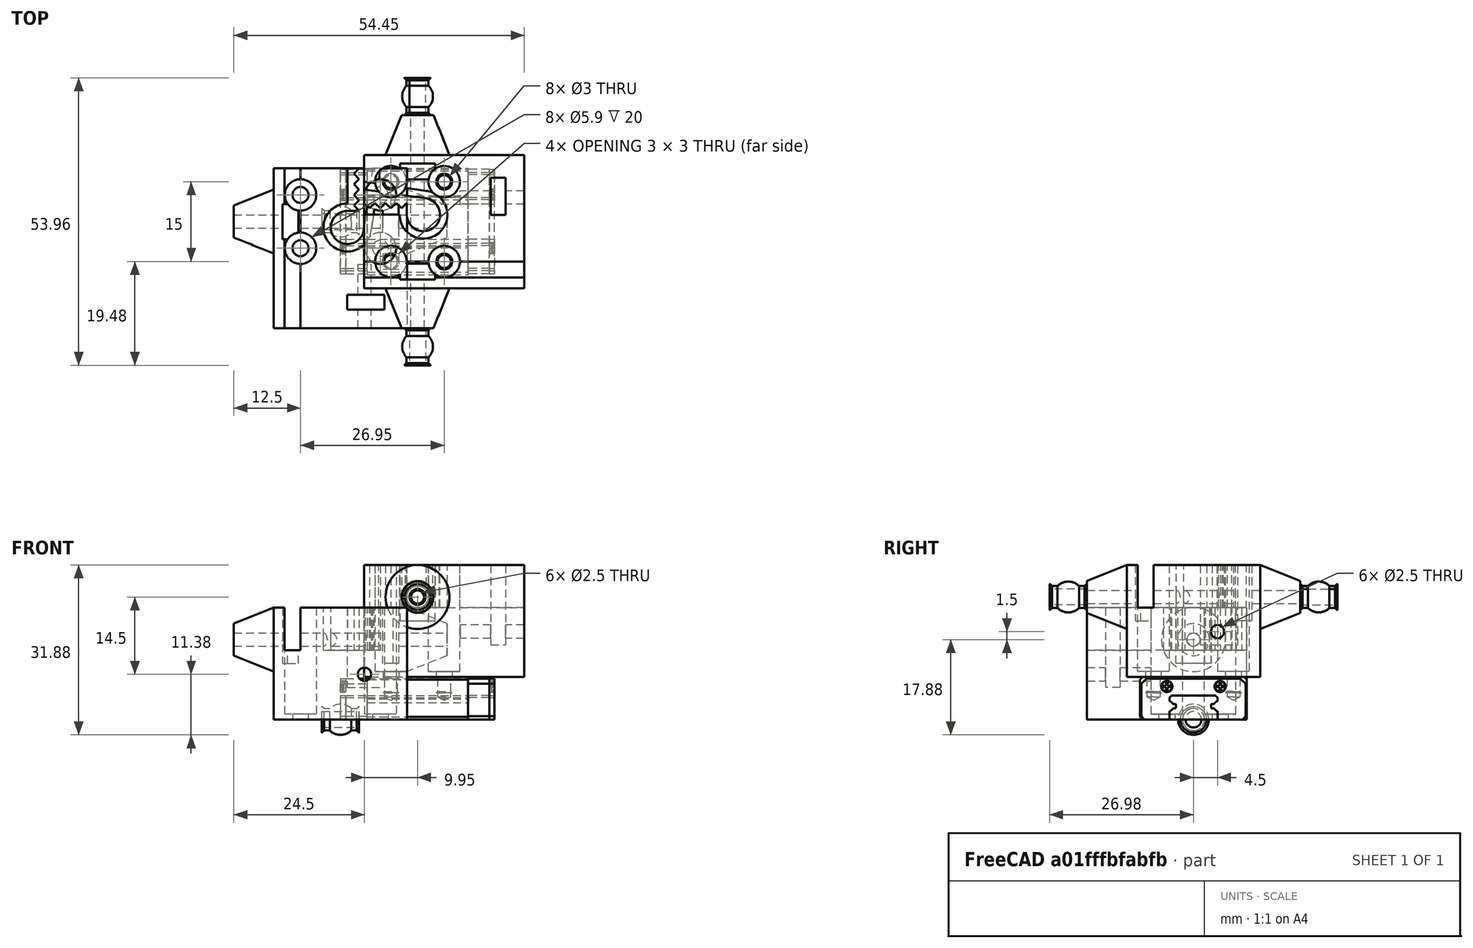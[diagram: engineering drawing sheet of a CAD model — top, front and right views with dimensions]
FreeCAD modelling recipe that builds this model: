
FCSTD DOCUMENT  (FreeCAD 2022.430R26244 +4758 (Git))
Label: SubAs3kossel_carriage_MGN9C
License: All rights reserved
LicenseURL: http://en.wikipedia.org/wiki/All_rights_reserved
objects: Part::Feature×21, Part::FeaturePython×16, App::FeaturePython×16, App::Link×7, App::LinkGroup×2, App::DocumentObjectGroup×2, App::LinkElement×2
note: 36 computed .brp shape members not serialized (recipe doc carries the construction recipe); baked Part::Feature solids carry a one-line shape summary decoded from their .brp
EXTERNAL_REF file=as3MGN9CZFC-HiwinCorporation-3D-10-31-2021.FCStd obj=Assembly
EXTERNAL_REF file=as3carriage_MGN9C.FCStd obj=Assembly

FEATURE [App::Link] Link  label="As3MGN9CZFC-HiwinCorporation-3D-10-31-2021"
  AutoLinkLabel = false
  AutoPlacement = true
  LinkedObject = -> <external as3MGN9CZFC-HiwinCorporation-3D-10-31-2021.FCStd>#Assembly
  SyncGroupVisibility = false
  TreeRank = 0
  _LinkOwner = 4486
  _LinkVersion = 1
FEATURE [App::Link] Link001  label="As3carriage_MGN9C"
  AutoLinkLabel = false
  AutoPlacement = true
  LinkPlacement = pos=(14.45,2.4e-15,8) rot=(0,0,1;1.5708rad)
  LinkedObject = -> <external as3carriage_MGN9C.FCStd>#Assembly
  Placement = pos=(14.45,2.4e-15,8) rot=(0,0,1;1.5708rad)
  SyncGroupVisibility = false
  TreeRank = 0
  _LinkOwner = 4486
  _LinkVersion = 1
FEATURE [Part::Feature] Solid  label="PRODUCT_NAME_1"
  TreeRank = 11
  shape: bbox 18.9 x 20 x 8 mm, 90 faces (baked)
FEATURE [Part::Feature] Solid001  label="PRODUCT_NAME_2"
  TreeRank = 12
  shape: bbox 4 x 19.6 x 7.7 mm, 40 faces (baked)
FEATURE [Part::Feature] Solid002  label="PRODUCT_NAME_3"
  TreeRank = 13
  shape: bbox 4 x 19.6 x 7.7 mm, 40 faces (baked)
FEATURE [Part::Feature] Solid003  label="PRODUCT_NAME_4"
  TreeRank = 14
  shape: bbox 1 x 19.6 x 7.7 mm, 46 faces (baked)
FEATURE [Part::Feature] Solid004  label="PRODUCT_NAME_5"
  TreeRank = 15
  shape: bbox 1 x 19.6 x 7.7 mm, 46 faces (baked)
FEATURE [Part::Feature] Solid005  label="PRODUCT_NAME_6"
  TreeRank = 16
  shape: bbox 0.9 x 2 x 2 mm, 18 faces (baked)
FEATURE [Part::Feature] Solid006  label="PRODUCT_NAME_7"
  TreeRank = 17
  shape: bbox 0.9 x 2 x 2 mm, 18 faces (baked)
FEATURE [Part::Feature] Solid007  label="PRODUCT_NAME_8"
  TreeRank = 18
  shape: bbox 0.9 x 2 x 2 mm, 18 faces (baked)
FEATURE [Part::Feature] Solid008  label="PRODUCT_NAME_9"
  TreeRank = 19
  shape: bbox 0.9 x 2 x 2 mm, 18 faces (baked)
FEATURE [App::LinkGroup] LinkGroup
  ElementList = -> [Solid,Solid001,Solid002,Solid003,Solid004,Solid005,Solid006,Solid007,Solid008]
  LinkMode = 0
  TreeRank = 36
  _LinkVersion = 1
FEATURE [Part::Feature] Solid009  label="carriage_MGN9C"
  TreeRank = 37
  shape: bbox 40 x 30 x 21 mm, 75 faces (baked)
FEATURE [App::Link] Link004  label="Link004(As3MGN9CZFC-HiwinCorporation-3D-10-31-2021)"
  AutoLinkLabel = true
  AutoPlacement = true
  LinkedObject = -> Link
  SyncGroupVisibility = false
  TreeRank = 38
  _LinkVersion = 1
FEATURE [App::Link] Link005  label="Link005(As3carriage_MGN9C)"
  AutoLinkLabel = true
  AutoPlacement = true
  LinkPlacement = pos=(14.45,-2.64669e-11,8) rot=(0,0,1;1.5708rad)
  LinkedObject = -> Link001
  Placement = pos=(14.45,-2.64669e-11,8) rot=(0,0,1;1.5708rad)
  SyncGroupVisibility = false
  TreeRank = 39
  _LinkVersion = 1
FEATURE [Part::Feature] Solid010  label="PRODUCT_NAME_010"
  TreeRank = 11
  shape: bbox 18.9 x 20 x 8 mm, 90 faces (baked)
FEATURE [Part::Feature] Solid011  label="PRODUCT_NAME_011"
  TreeRank = 12
  shape: bbox 4 x 19.6 x 7.7 mm, 40 faces (baked)
FEATURE [Part::Feature] Solid012  label="PRODUCT_NAME_012"
  TreeRank = 13
  shape: bbox 4 x 19.6 x 7.7 mm, 40 faces (baked)
FEATURE [Part::Feature] Solid013  label="PRODUCT_NAME_013"
  TreeRank = 14
  shape: bbox 1 x 19.6 x 7.7 mm, 46 faces (baked)
FEATURE [Part::Feature] Solid014  label="PRODUCT_NAME_014"
  TreeRank = 15
  shape: bbox 1 x 19.6 x 7.7 mm, 46 faces (baked)
FEATURE [Part::Feature] Solid015  label="PRODUCT_NAME_015"
  TreeRank = 16
  shape: bbox 0.9 x 2 x 2 mm, 18 faces (baked)
FEATURE [Part::Feature] Solid016  label="PRODUCT_NAME_016"
  TreeRank = 17
  shape: bbox 0.9 x 2 x 2 mm, 18 faces (baked)
FEATURE [Part::Feature] Solid017  label="PRODUCT_NAME_017"
  TreeRank = 18
  shape: bbox 0.9 x 2 x 2 mm, 18 faces (baked)
FEATURE [Part::Feature] Solid018  label="PRODUCT_NAME_018"
  TreeRank = 19
  shape: bbox 0.9 x 2 x 2 mm, 18 faces (baked)
FEATURE [App::LinkGroup] LinkGroup001
  ElementList = -> [Solid010,Solid011,Solid012,Solid013,Solid014,Solid015,Solid016,Solid017,Solid018]
  LinkMode = 0
  TreeRank = 35
  _LinkVersion = 1
FEATURE [Part::Feature] Solid019  label="carriage_MGN9C001"
  TreeRank = 34
  shape: bbox 40 x 30 x 21 mm, 75 faces (baked)
FEATURE [App::Link] Link008  label="Link008(As3MGN9CZFC-HiwinCorporation-3D-10-31-2021)"
  AutoLinkLabel = true
  AutoPlacement = true
  LinkedObject = -> Link
  SyncGroupVisibility = false
  TreeRank = 32
  _LinkVersion = 1
FEATURE [App::Link] Link009  label="Link009(As3carriage_MGN9C)"
  AutoLinkLabel = true
  AutoPlacement = true
  LinkPlacement = pos=(14.45,-2.64669e-11,8) rot=(0,0,1;1.5708rad)
  LinkedObject = -> Link001
  Placement = pos=(14.45,-2.64669e-11,8) rot=(0,0,1;1.5708rad)
  SyncGroupVisibility = false
  TreeRank = 33
  _LinkVersion = 1
FEATURE [App::DocumentObjectGroup] Group  label="Groupe"
  ClaimAllChildren = true
  ExportMode = 1
  Group = -> [LinkGroup,Solid009,Link004,Link005]
  TreeRank = 40
  _GroupVersion = 1
FEATURE [App::DocumentObjectGroup] Group001  label="Groupe001"
  ClaimAllChildren = true
  ExportMode = 1
  Group = -> [Solid019,LinkGroup001,Link008,Link009]
  TreeRank = 41
  _GroupVersion = 1
FEATURE [App::LinkElement] Link010_i0
  LinkPlacement = pos=(14.45,23.49,23) rot=(0,0,1;1.5708rad)
  LinkedObject = -> Solid020
  Placement = pos=(14.45,23.49,23) rot=(0,0,1;1.5708rad)
  TreeRank = 46
  _LinkOwner = 4607
  _LinkVersion = 1
FEATURE [App::LinkElement] Link010_i1
  LinkPlacement = pos=(14.45,-23.49,23) rot=(0,0,-1;1.5708rad)
  LinkedObject = -> Solid020
  Placement = pos=(14.45,-23.49,23) rot=(0,0,-1;1.5708rad)
  TreeRank = 47
  _LinkOwner = 4607
  _LinkVersion = 1
FEATURE [App::Link] Link010  label="As3Traxxas5347ball"
  AutoLinkLabel = false
  AutoPlacement = true
  ElementCount = 2
  ElementList = -> [Link010_i0,Link010_i1]
  LinkedObject = -> Solid020
  SyncGroupVisibility = false
  TreeRank = 45
  _LinkOwner = 4486
  _LinkVersion = 1
FEATURE [Part::FeaturePython] Parts  # WARN: FeaturePython — macro-defined, semantics opaque (R4)
  Group = -> [Link,Link001,Link010]
  GroupMode = 0
  TreeRank = 0
  _LinkVersion = 1
FEATURE [Part::Feature] Solid020  label="5347 ball"
  TreeRank = 66
  shape: bbox 6.98 x 5.77 x 5.77 mm, 10 faces (baked)
FEATURE [Part::FeaturePython] Assembly  label="SubAs3kossel_carriage_MGN9C"  # WARN: FeaturePython — macro-defined, semantics opaque (R4)
  AutoRelax = true
  BuildShape = 0
  Freeze = true
  Group = -> [Constraints,Elements,Parts]
  TreeRank = 0
  Verbose = false
  _LinkVersion = 1
  _SolverType = 1
  _Version = 1
FEATURE [App::FeaturePython] Constraints  # WARN: FeaturePython — macro-defined, semantics opaque (R4)
  Group = -> [Constraint,Constraint001,Constraint003,Constraint004,Constraint005]
  TreeRank = 0
  _LinkVersion = 1
  _Version = 1
FEATURE [App::FeaturePython] Elements  # WARN: FeaturePython — macro-defined, semantics opaque (R4)
  Group = -> [_Element,_Element001,_Element003,_Element004,_Element005,Element,_Element006,_Element007,_Element008,_Element009,_Element010,_Element011,Element001,Element002]
  TreeRank = 0
  _LinkVersion = 1
FEATURE [App::FeaturePython] Constraint  label="Locked"  # WARN: FeaturePython — macro-defined, semantics opaque (R4)
  Disabled = false
  Group = -> [ElementLink]
  TreeRank = 0
  _ConstraintType = 0
  _LinkVersion = 1
  _Parent = -> Constraints
FEATURE [App::FeaturePython] ElementLink  label="Ref@As3MGN9CZFC-HiwinCorporation-3D-10-31-2021@"  # link proxy (typed FeaturePython)
  LinkTransform = true
  LinkedObject = -> _Element
  TreeRank = 0
  _LinkVersion = 1
  _Parent = -> Constraint
FEATURE [Part::FeaturePython] _Element  label="Ref@As3MGN9CZFC-HiwinCorporation-3D-10-31-2021@"  # link proxy (typed FeaturePython)
  Detach = false
  LinkTransform = true
  LinkedObject = -> Link [1.$Ref.]
  TreeRank = 0
  _LinkVersion = 1
  _Parent = -> Elements
FEATURE [Part::FeaturePython] _Element001  label="Fix1@As3MGN9CZFC-HiwinCorporation-3D-10-31-2021@"  # link proxy (typed FeaturePython)
  Detach = false
  LinkTransform = true
  LinkedObject = -> Link [1.$Fix1.]
  TreeRank = 0
  _LinkVersion = 1
  _Parent = -> Elements
FEATURE [Part::FeaturePython] _Element003  label="Fix2@As3MGN9CZFC-HiwinCorporation-3D-10-31-2021@"  # link proxy (typed FeaturePython)
  Detach = false
  LinkTransform = true
  LinkedObject = -> Link [1.$Fix2.]
  TreeRank = 0
  _LinkVersion = 1
  _Parent = -> Elements
FEATURE [App::FeaturePython] Constraint001  label="PlaneCoincident"  # WARN: FeaturePython — macro-defined, semantics opaque (R4)
  Angle = 0
  AnglePitch = 0
  AngleRoll = 0
  Cascade = false
  Disabled = false
  Group = -> [ElementLink001,ElementLink002]
  LockAngle = false
  Multiply = false
  OffsetX = 0
  OffsetY = 0
  TreeRank = 0
  _ConstraintType = 35
  _LinkVersion = 1
  _Parent = -> Constraints
FEATURE [App::FeaturePython] ElementLink001  label="Fix1@As3MGN9CZFC-HiwinCorporation-3D-10-31-2021@"  # link proxy (typed FeaturePython)
  LinkTransform = true
  LinkedObject = -> _Element001
  TreeRank = 0
  _LinkVersion = 1
  _Parent = -> Constraint001
FEATURE [App::FeaturePython] ElementLink002  label="Fix1@As3carriage_MGN9C@"  # link proxy (typed FeaturePython)
  LinkTransform = true
  LinkedObject = -> _Element004
  Offset = pos=(0,0,0) rot=(1,0,0;3.14159rad)
  Placement = pos=(38.9,-2.0572e-11,16) rot=(0,1,0;3.14159rad)
  TreeRank = 0
  _LinkVersion = 1
  _Parent = -> Constraint001
FEATURE [Part::FeaturePython] _Element004  label="Fix1@As3carriage_MGN9C@"  # link proxy (typed FeaturePython)
  Detach = false
  LinkTransform = true
  LinkedObject = -> Link001 [1.$Fix1.]
  TreeRank = 0
  _LinkVersion = 1
  _Parent = -> Elements
FEATURE [Part::FeaturePython] _Element005  label="Fix2@As3carriage_MGN9C@"  # link proxy (typed FeaturePython)
  Detach = false
  LinkTransform = true
  LinkedObject = -> Link001 [1.$Fix2.]
  TreeRank = 0
  _LinkVersion = 1
  _Parent = -> Elements
FEATURE [Part::FeaturePython] Element  label="Lat@As3MGN9CZFC-HiwinCorporation-3D-10-31-2021@"  # link proxy (typed FeaturePython)
  Detach = false
  LinkTransform = true
  LinkedObject = -> Link [1.$Lat.]
  TreeRank = 42
  _LinkVersion = 1
  _Parent = -> Elements
FEATURE [App::FeaturePython] Constraint003  label="SameOrientation"  # WARN: FeaturePython — macro-defined, semantics opaque (R4)
  Disabled = false
  Group = -> [ElementLink005,ElementLink006]
  TreeRank = 49
  _ConstraintType = 2
  _LinkVersion = 1
  _Parent = -> Constraints
FEATURE [App::FeaturePython] ElementLink005  label="_Element006"  # link proxy (typed FeaturePython)
  LinkTransform = true
  LinkedObject = -> _Element006
  TreeRank = 50
  _LinkVersion = 1
  _Parent = -> Constraint003
FEATURE [Part::FeaturePython] _Element006  # link proxy (typed FeaturePython)
  Detach = false
  LinkTransform = true
  LinkedObject = -> Link001 [1.$Element006.]
  TreeRank = 51
  _LinkVersion = 1
  _Parent = -> Elements
FEATURE [App::FeaturePython] ElementLink006  label="_Element007"  # link proxy (typed FeaturePython)
  LinkTransform = true
  LinkedObject = -> _Element007
  TreeRank = 52
  _LinkVersion = 1
  _Parent = -> Constraint003
FEATURE [Part::FeaturePython] _Element007  # link proxy (typed FeaturePython)
  Detach = false
  LinkTransform = true
  LinkedObject = -> Link [1.$Element004.]
  TreeRank = 53
  _LinkVersion = 1
  _Parent = -> Elements
FEATURE [App::FeaturePython] Constraint004  label="Attachment"  # WARN: FeaturePython — macro-defined, semantics opaque (R4)
  Cascade = false
  Disabled = false
  Group = -> [ElementLink007,ElementLink008]
  Multiply = false
  TreeRank = 54
  _ConstraintType = 45
  _LinkVersion = 1
  _Parent = -> Constraints
FEATURE [App::FeaturePython] ElementLink007  label="Rot1@As3carriage_MGN9C@"  # link proxy (typed FeaturePython)
  LinkTransform = true
  LinkedObject = -> _Element008
  TreeRank = 55
  _LinkVersion = 1
  _Parent = -> Constraint004
FEATURE [Part::FeaturePython] _Element008  label="Rot1@As3carriage_MGN9C@"  # link proxy (typed FeaturePython)
  Detach = false
  LinkTransform = true
  LinkedObject = -> Link001 [1.$Rot1.]
  TreeRank = 56
  _LinkVersion = 1
  _Parent = -> Elements
FEATURE [App::FeaturePython] ElementLink008  label="ElCircle@As3Traxxas5347ball@#0"  # link proxy (typed FeaturePython)
  LinkTransform = true
  LinkedObject = -> _Element009
  TreeRank = 57
  _LinkVersion = 1
  _Parent = -> Constraint004
FEATURE [Part::FeaturePython] _Element009  label="ElCircle@As3Traxxas5347ball@#0"  # link proxy (typed FeaturePython)
  Detach = false
  LinkTransform = true
  LinkedObject = -> Link010 [Link010_i0.Edge10]
  TreeRank = 58
  _LinkVersion = 1
  _Parent = -> Elements
FEATURE [App::FeaturePython] Constraint005  label="Attachment001"  # WARN: FeaturePython — macro-defined, semantics opaque (R4)
  Cascade = false
  Disabled = false
  Group = -> [ElementLink009,ElementLink010]
  Multiply = false
  TreeRank = 59
  _ConstraintType = 45
  _LinkVersion = 1
  _Parent = -> Constraints
FEATURE [App::FeaturePython] ElementLink009  label="Rot2@As3carriage_MGN9C@"  # link proxy (typed FeaturePython)
  LinkTransform = true
  LinkedObject = -> _Element010
  TreeRank = 60
  _LinkVersion = 1
  _Parent = -> Constraint005
FEATURE [Part::FeaturePython] _Element010  label="Rot2@As3carriage_MGN9C@"  # link proxy (typed FeaturePython)
  Detach = false
  LinkTransform = true
  LinkedObject = -> Link001 [1.$Rot2.]
  TreeRank = 61
  _LinkVersion = 1
  _Parent = -> Elements
FEATURE [App::FeaturePython] ElementLink010  label="ElCircle@As3Traxxas5347ball@#1"  # link proxy (typed FeaturePython)
  LinkTransform = true
  LinkedObject = -> _Element011
  TreeRank = 62
  _LinkVersion = 1
  _Parent = -> Constraint005
FEATURE [Part::FeaturePython] _Element011  label="ElCircle@As3Traxxas5347ball@#1"  # link proxy (typed FeaturePython)
  Detach = false
  LinkTransform = true
  LinkedObject = -> Link010 [Link010_i1.Edge10]
  TreeRank = 63
  _LinkVersion = 1
  _Parent = -> Elements
FEATURE [Part::FeaturePython] Element001  label="ElSphereM@As3Traxxas5347ball@#0"  # link proxy (typed FeaturePython)
  Detach = false
  LinkTransform = true
  LinkedObject = -> Link010 [Link010_i0.Face8]
  TreeRank = 64
  _LinkVersion = 1
  _Parent = -> Elements
FEATURE [Part::FeaturePython] Element002  label="ElSphereM@As3Traxxas5347ball@#1"  # link proxy (typed FeaturePython)
  Detach = false
  LinkTransform = true
  LinkedObject = -> Link010 [Link010_i1.Face8]
  TreeRank = 65
  _LinkVersion = 1
  _Parent = -> Elements

RESOLVED EXTERNAL PARTS (link-assembly join: the EXTERNAL_REF files above that resolve inside this repo's crawl, each included once):
---- part as3MGN9CZFC-HiwinCorporation-3D-10-31-2021.FCStd = doc fcstd_e7517699af7a ----
FCSTD DOCUMENT  (FreeCAD 2022.430R26244 +4758 (Git))
Label: as3MGN9CZFC-HiwinCorporation-3D-10-31-2021
License: All rights reserved
LicenseURL: http://en.wikipedia.org/wiki/All_rights_reserved
objects: Part::Feature×9, Part::FeaturePython×7, App::FeaturePython×2, App::LinkGroup×1
note: 15 computed .brp shape members not serialized (recipe doc carries the construction recipe); baked Part::Feature solids carry a one-line shape summary decoded from their .brp

FEATURE [App::FeaturePython] Constraints  # WARN: FeaturePython — macro-defined, semantics opaque (R4)
  TreeRank = 0
  _LinkVersion = 1
  _Version = 1
FEATURE [Part::Feature] Solid  label="PRODUCT_NAME_1"
  TreeRank = 11
  shape: bbox 18.9 x 20 x 8 mm, 90 faces (baked)
FEATURE [Part::Feature] Solid001  label="PRODUCT_NAME_2"
  TreeRank = 12
  shape: bbox 4 x 19.6 x 7.7 mm, 40 faces (baked)
FEATURE [Part::Feature] Solid002  label="PRODUCT_NAME_3"
  TreeRank = 13
  shape: bbox 4 x 19.6 x 7.7 mm, 40 faces (baked)
FEATURE [Part::Feature] Solid003  label="PRODUCT_NAME_4"
  TreeRank = 14
  shape: bbox 1 x 19.6 x 7.7 mm, 46 faces (baked)
FEATURE [Part::Feature] Solid004  label="PRODUCT_NAME_5"
  TreeRank = 15
  shape: bbox 1 x 19.6 x 7.7 mm, 46 faces (baked)
FEATURE [Part::Feature] Solid005  label="PRODUCT_NAME_6"
  TreeRank = 16
  shape: bbox 0.9 x 2 x 2 mm, 18 faces (baked)
FEATURE [Part::Feature] Solid006  label="PRODUCT_NAME_7"
  TreeRank = 17
  shape: bbox 0.9 x 2 x 2 mm, 18 faces (baked)
FEATURE [Part::Feature] Solid007  label="PRODUCT_NAME_8"
  TreeRank = 18
  shape: bbox 0.9 x 2 x 2 mm, 18 faces (baked)
FEATURE [Part::Feature] Solid008  label="PRODUCT_NAME_9"
  TreeRank = 19
  shape: bbox 0.9 x 2 x 2 mm, 18 faces (baked)
FEATURE [App::LinkGroup] LinkGroup
  ElementList = -> [Solid,Solid001,Solid002,Solid003,Solid004,Solid005,Solid006,Solid007,Solid008]
  LinkMode = 0
  TreeRank = 20
  _LinkVersion = 1
FEATURE [Part::FeaturePython] Parts  # WARN: FeaturePython — macro-defined, semantics opaque (R4)
  Group = -> [LinkGroup]
  GroupMode = 0
  TreeRank = 0
  _LinkVersion = 1
FEATURE [Part::FeaturePython] Assembly  label="As3MGN9CZFC-HiwinCorporation-3D-10-31-2021"  # WARN: FeaturePython — macro-defined, semantics opaque (R4)
  AutoRelax = true
  BuildShape = 0
  Freeze = true
  Group = -> [Constraints,Elements,Parts]
  TreeRank = 0
  Verbose = false
  _LinkVersion = 1
  _SolverType = 1
  _Version = 1
FEATURE [App::FeaturePython] Elements  # WARN: FeaturePython — macro-defined, semantics opaque (R4)
  Group = -> [Element,Element001,Element002,Element003,Element004]
  TreeRank = 0
  _LinkVersion = 1
FEATURE [Part::FeaturePython] Element  label="Ref"  # link proxy (typed FeaturePython)
  Detach = false
  LinkTransform = true
  LinkedObject = -> LinkGroup [Solid.Face79]
  TreeRank = 21
  _LinkVersion = 1
  _Parent = -> Elements
FEATURE [Part::FeaturePython] Element001  label="Fix1"  # link proxy (typed FeaturePython)
  Detach = false
  LinkTransform = true
  LinkedObject = -> LinkGroup [Solid.Edge201]
  TreeRank = 22
  _LinkVersion = 1
  _Parent = -> Elements
FEATURE [Part::FeaturePython] Element002  label="Fix2"  # link proxy (typed FeaturePython)
  Detach = false
  LinkTransform = true
  LinkedObject = -> LinkGroup [Solid.Edge57]
  TreeRank = 23
  _LinkVersion = 1
  _Parent = -> Elements
FEATURE [Part::FeaturePython] Element003  label="Lat"  # link proxy (typed FeaturePython)
  Detach = false
  LinkTransform = true
  LinkedObject = -> LinkGroup [Solid.Face37]
  TreeRank = 24
  _LinkVersion = 1
  _Parent = -> Elements
FEATURE [Part::FeaturePython] Element004  # link proxy (typed FeaturePython)
  Detach = false
  LinkTransform = true
  LinkedObject = -> LinkGroup [Solid004.Face43]
  TreeRank = 25
  _LinkVersion = 1
  _Parent = -> Elements
---- part as3carriage_MGN9C.FCStd = doc fcstd_92dfbb5098b0 ----
FCSTD DOCUMENT  (FreeCAD 2022.430R26244 +4758 (Git))
Label: as3carriage_MGN9C
License: All rights reserved
LicenseURL: http://en.wikipedia.org/wiki/All_rights_reserved
objects: Part::FeaturePython×7, App::FeaturePython×2, Part::Feature×1
note: 7 computed .brp shape members not serialized (recipe doc carries the construction recipe); baked Part::Feature solids carry a one-line shape summary decoded from their .brp

FEATURE [Part::Feature] Solid  label="carriage_MGN9C"
  TreeRank = 0
  shape: bbox 40 x 30 x 21 mm, 75 faces (baked)
FEATURE [App::FeaturePython] Constraints  # WARN: FeaturePython — macro-defined, semantics opaque (R4)
  TreeRank = 0
  _LinkVersion = 1
  _Version = 1
FEATURE [Part::FeaturePython] Parts  # WARN: FeaturePython — macro-defined, semantics opaque (R4)
  Group = -> [Solid]
  GroupMode = 0
  TreeRank = 0
  _LinkVersion = 1
FEATURE [Part::FeaturePython] Assembly  label="As3carriage_MGN9C"  # WARN: FeaturePython — macro-defined, semantics opaque (R4)
  AutoRelax = true
  BuildShape = 0
  Freeze = false
  Group = -> [Constraints,Elements,Parts]
  TreeRank = 0
  Verbose = false
  _LinkVersion = 1
  _SolverType = 1
  _Version = 1
FEATURE [App::FeaturePython] Elements  # WARN: FeaturePython — macro-defined, semantics opaque (R4)
  Group = -> [Element,Element003,Element004,Element005,Element006]
  TreeRank = 0
  _LinkVersion = 1
FEATURE [Part::FeaturePython] Element  label="Fix1"  # link proxy (typed FeaturePython)
  Detach = false
  LinkTransform = true
  LinkedObject = -> Solid [Edge20]
  TreeRank = 0
  _LinkVersion = 1
  _Parent = -> Elements
FEATURE [Part::FeaturePython] Element003  label="Fix2"  # link proxy (typed FeaturePython)
  Detach = false
  LinkTransform = true
  LinkedObject = -> Solid [Edge21]
  TreeRank = 0
  _LinkVersion = 1
  _Parent = -> Elements
FEATURE [Part::FeaturePython] Element004  label="Rot1"  # link proxy (typed FeaturePython)
  Detach = false
  LinkTransform = true
  LinkedObject = -> Solid [Edge200]
  TreeRank = 0
  _LinkVersion = 1
  _Parent = -> Elements
FEATURE [Part::FeaturePython] Element005  label="Rot2"  # link proxy (typed FeaturePython)
  Detach = false
  LinkTransform = true
  LinkedObject = -> Solid [Edge213]
  TreeRank = 0
  _LinkVersion = 1
  _Parent = -> Elements
FEATURE [Part::FeaturePython] Element006  # link proxy (typed FeaturePython)
  Detach = false
  LinkTransform = true
  LinkedObject = -> Solid [Face17]
  TreeRank = 0
  _LinkVersion = 1
  _Parent = -> Elements
